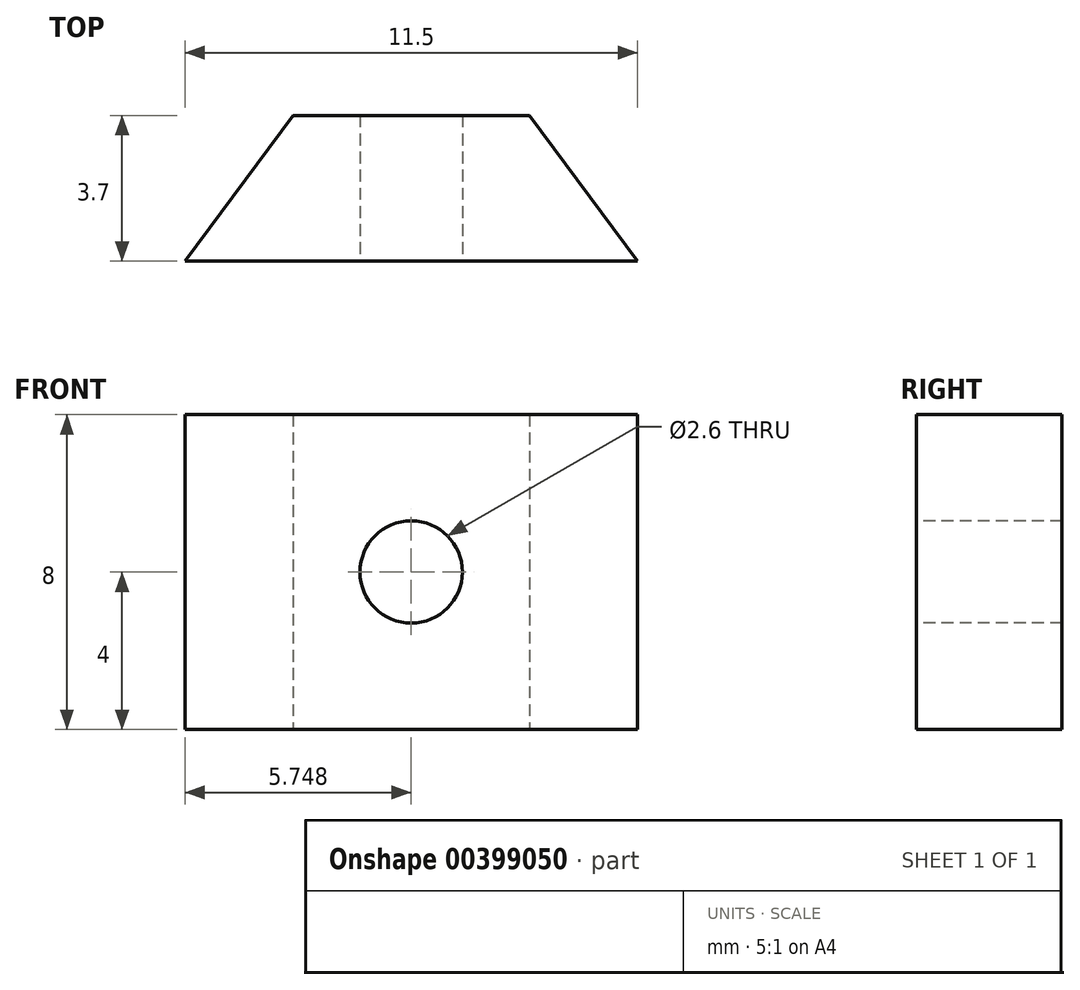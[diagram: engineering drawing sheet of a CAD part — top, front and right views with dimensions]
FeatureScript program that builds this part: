
annotation { "Feature Type Name" : "Feature", "Feature Type Description" : "" }
export const myFeature = defineFeature(function(context is Context, id is Id, definition is map)
    precondition{}
    {
        {
            var Q0;
            Q0=qCreatedBy(makeId("Top.planeOp"),FACE);
            var sketch = newSketch(context, id + "F0", { "sketchPlane" : qUnion([Q0])});
            skLineSegment(sketch, "E0", {"start": v(4.6, 3.49) * mm, "end": v(16.1, 3.49) * mm});
            skLineSegment(sketch, "E1", {"start": v(7.36, 7.19) * mm, "end": v(13.36, 7.19) * mm});
            skPoint(sketch, "E2.start.orphan", {"position": v(10.36, 7.19) * mm});
            skPoint(sketch, "E3.start.orphan", {"position": v(10.36, 3.49) * mm});
            skLineSegment(sketch, "E4", {"start": v(4.6, 3.49) * mm, "end": v(7.36, 7.19) * mm});
            skLineSegment(sketch, "E5", {"start": v(13.36, 7.19) * mm, "end": v(16.1, 3.49) * mm});
            skSolve(sketch);
        }
        {
            var Q0;
            Q0 = qSketchRegion(id + "F0", true);
            extrude(context, id + "F1", {"entities" : qUnion([Q0]), "depth" : 8 * mm});
        }
        {
            var Q0;
            Q0=makeQuery(id+"F1.opExtrude","SWEPT_FACE",FACE,{"disambiguationData":[OSD([sQuery(id+"F0.wireOp",EDGE,"E0")])]});
            var sketch = newSketch(context, id + "F2", { "sketchPlane" : qUnion([Q0])});
            skCircle(sketch, "E6", {"center": v(10.36, 4) * mm, "radius": 1.3 * mm});
            skPoint(sketch, "E6.centerSnap0", {"position": v(16.1, 4) * mm});
            skPoint(sketch, "E6.centerSnap1", {"position": v(10.36, 8) * mm});
            skSolve(sketch);
        }
        {
            var Q0;
            Q0 = qSketchRegion(id + "F2", true);
            extrude(context, id + "F3", {"entities" : qUnion([Q0]), "operationType" : NewBodyOperationType.REMOVE, "endBound" : BoundingType.THROUGH_ALL, "oppositeDirection" : true, "depth" : 25 * mm});
        }
    });
